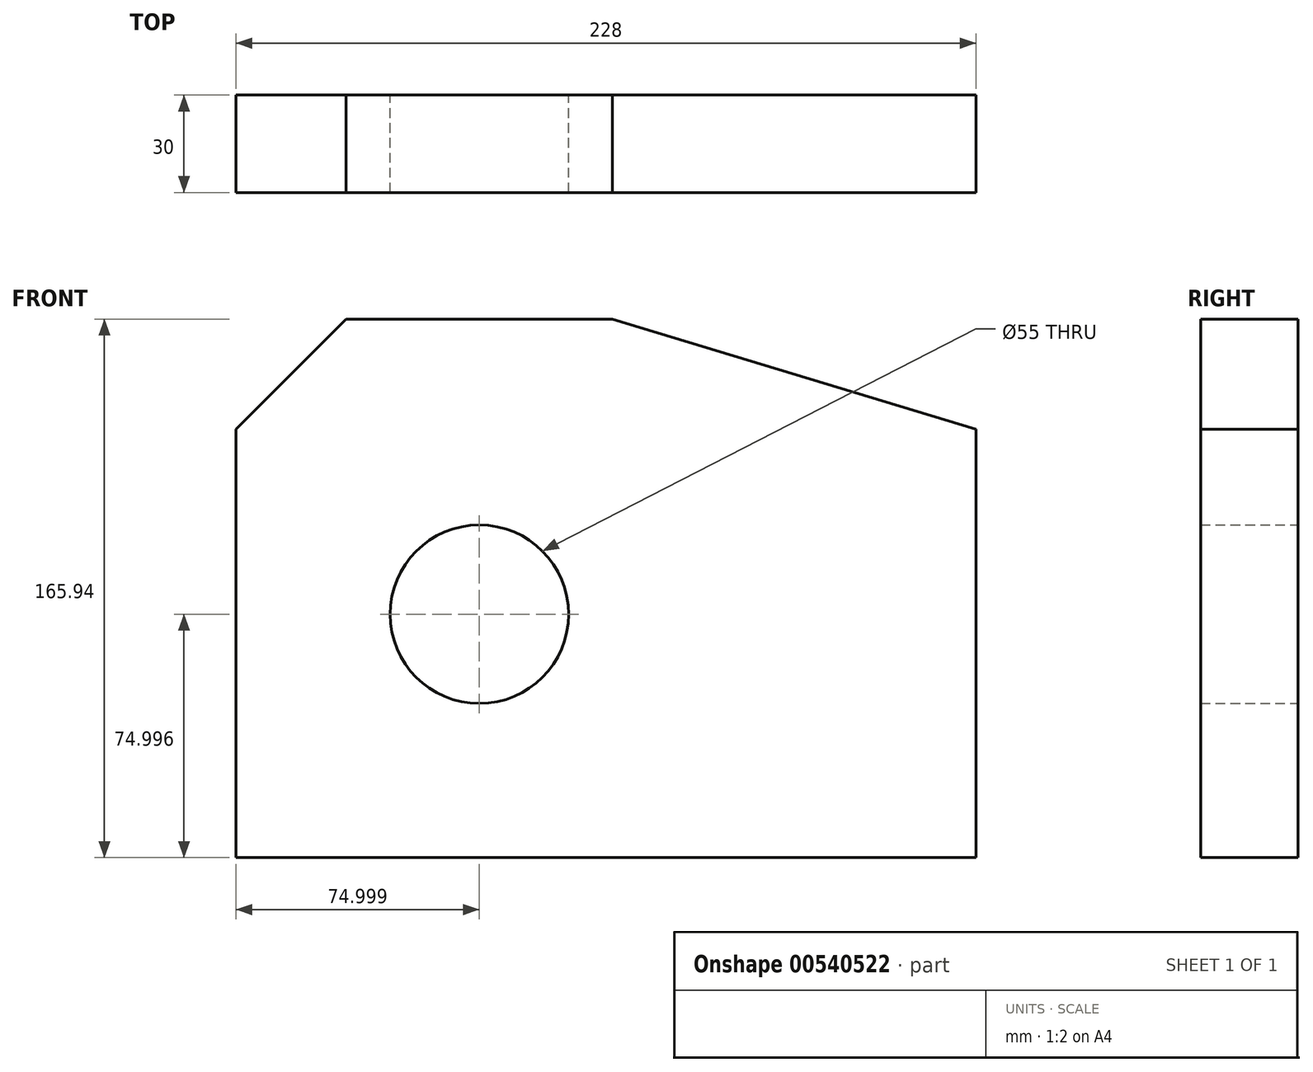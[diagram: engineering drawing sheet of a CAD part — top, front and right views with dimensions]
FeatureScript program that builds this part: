
annotation { "Feature Type Name" : "Feature", "Feature Type Description" : "" }
export const myFeature = defineFeature(function(context is Context, id is Id, definition is map)
    precondition{}
    {
        {
            var Q0;
            Q0=qCreatedBy(makeId("Front.planeOp"),FACE);
            var sketch = newSketch(context, id + "F0", { "sketchPlane" : qUnion([Q0])});
            skLineSegment(sketch, "E0", {"start": v(-104.97, 34.62) * mm, "end": v(-71.03, 68.56) * mm});
            skLineSegment(sketch, "E1", {"start": v(-71.03, 68.56) * mm, "end": v(11.06, 68.56) * mm});
            skLineSegment(sketch, "E2", {"start": v(11.06, 68.56) * mm, "end": v(123.03, 34.62) * mm});
            skLineSegment(sketch, "E3", {"start": v(123.03, 34.62) * mm, "end": v(123.03, -97.38) * mm});
            skLineSegment(sketch, "E4", {"start": v(123.03, -97.38) * mm, "end": v(-104.97, -97.38) * mm});
            skLineSegment(sketch, "E5", {"start": v(-104.97, -97.38) * mm, "end": v(-104.97, 34.62) * mm});
            skCircle(sketch, "E6", {"center": v(-29.97, -22.38) * mm, "radius": 27.5 * mm});
            skLineSegment(sketch, "E7", {"start": v(-29.97, -22.38) * mm, "end": v(-127.07, -22.38) * mm});
            skSolve(sketch);
        }
        {
            var Q0;
            Q0 = qSketchRegion(id + "F0", true);
            extrude(context, id + "F1", {"entities" : qUnion([Q0]), "depth" : 30 * mm, "offsetDistance" : 25 * mm});
        }
    });
